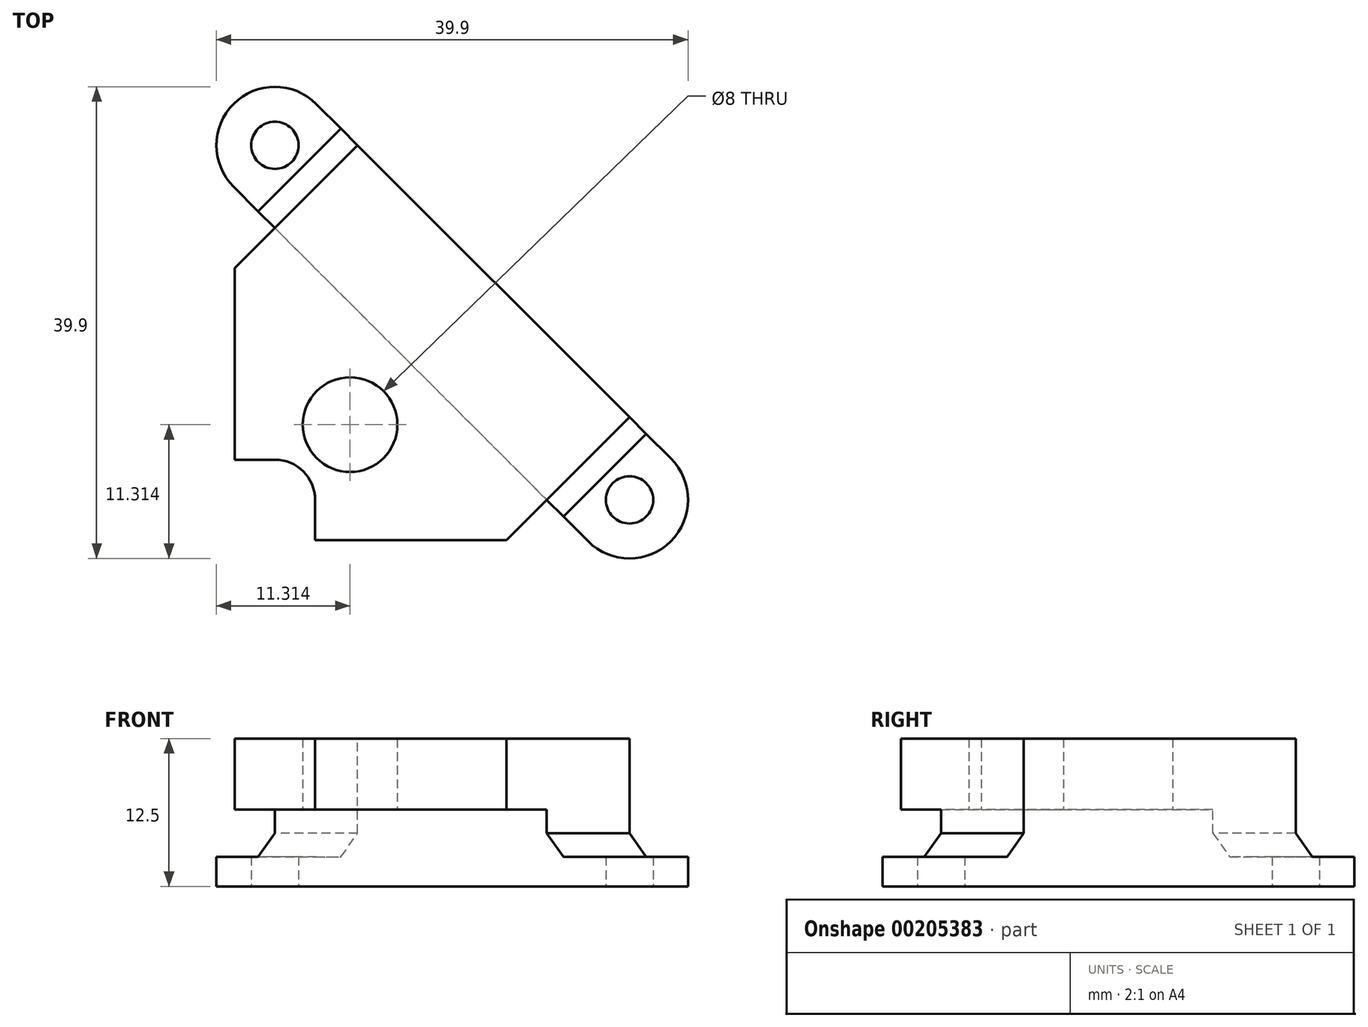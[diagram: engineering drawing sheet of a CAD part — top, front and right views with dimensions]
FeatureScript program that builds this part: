
annotation { "Feature Type Name" : "Feature", "Feature Type Description" : "" }
export const myFeature = defineFeature(function(context is Context, id is Id, definition is map)
    precondition{}
    {
        {
            var Q0;
            Q0=qCreatedBy(makeId("Top.planeOp"),FACE);
            var sketch = newSketch(context, id + "F0", { "sketchPlane" : qUnion([Q0])});
            skLineSegment(sketch, "E0.bottom", {"start": v(0, 0) * mm, "end": v(37, 0) * mm, "construction": true});
            skLineSegment(sketch, "E0.top", {"start": v(0, 37) * mm, "end": v(37, 37) * mm, "construction": true});
            skLineSegment(sketch, "E0.left", {"start": v(0, 0) * mm, "end": v(0, 37) * mm, "construction": true});
            skLineSegment(sketch, "E0.right", {"start": v(37, 0) * mm, "end": v(37, 37) * mm, "construction": true});
            skCircle(sketch, "E1", {"center": v(3.5, 33.5) * mm, "radius": 3 * mm, "construction": true});
            skCircle(sketch, "E2", {"center": v(33.5, 33.5) * mm, "radius": 3 * mm, "construction": true});
            skCircle(sketch, "E3", {"center": v(33.5, 3.5) * mm, "radius": 2.51 * mm, "construction": true});
            skCircle(sketch, "E4", {"center": v(3.5, 3.5) * mm, "radius": 3 * mm, "construction": true});
            skCircle(sketch, "E5", {"center": v(3.5, 33.5) * mm, "radius": 2 * mm});
            skCircle(sketch, "E6", {"center": v(33.5, 3.5) * mm, "radius": 2 * mm});
            skArc(sketch, "E7", {"start": v(7, 37) * mm, "mid": v(0, 37) * mm, "end": v(0, 30) * mm});
            skArc(sketch, "E8", {"start": v(30, 0) * mm, "mid": v(37, 0) * mm, "end": v(37, 7) * mm});
            skLineSegment(sketch, "E9", {"start": v(0, 30) * mm, "end": v(30, 0) * mm});
            skLineSegment(sketch, "E10", {"start": v(7, 37) * mm, "end": v(37, 7) * mm});
            skSolve(sketch);
        }
        {
            var Q0;
            Q0 = qSketchRegion(id + "F0", true);
            extrude(context, id + "F1", {"entities" : qUnion([Q0]), "depth" : 6.5 * mm});
        }
        {
            var Q0;
            Q0=makeQuery(id+"F1.opExtrude","CAP_FACE",FACE,{"disambiguationData":[OSD([sQuery(id+"F0.wireOp",EDGE,"E5"),sQuery(id+"F0.wireOp",EDGE,"E6"),sQuery(id+"F0.wireOp",EDGE,"E7"),sQuery(id+"F0.wireOp",EDGE,"E8"),sQuery(id+"F0.wireOp",EDGE,"E9"),sQuery(id+"F0.wireOp",EDGE,"E10")])],"isStart":false});
            var sketch = newSketch(context, id + "F2", { "sketchPlane" : qUnion([Q0])});
            skArc(sketch, "E11", {"start": v(7, 37) * mm, "mid": v(0, 37) * mm, "end": v(0, 30) * mm});
            skArc(sketch, "E12", {"start": v(30, 0) * mm, "mid": v(37, 0) * mm, "end": v(37, 7) * mm});
            skLineSegment(sketch, "E13", {"start": v(3.5, 26.5) * mm, "end": v(10.5, 33.5) * mm});
            skLineSegment(sketch, "E14", {"start": v(3.5, 26.5) * mm, "end": v(0, 30) * mm});
            skLineSegment(sketch, "E15", {"start": v(10.5, 33.5) * mm, "end": v(7, 37) * mm});
            skLineSegment(sketch, "E16", {"start": v(30, 0) * mm, "end": v(26.5, 3.5) * mm});
            skLineSegment(sketch, "E17", {"start": v(26.5, 3.5) * mm, "end": v(33.5, 10.5) * mm});
            skLineSegment(sketch, "E18", {"start": v(33.5, 10.5) * mm, "end": v(37, 7) * mm});
            skSolve(sketch);
        }
        {
            var Q0;
            Q0 = qSketchRegion(id + "F2", true);
            extrude(context, id + "F3", {"entities" : qUnion([Q0]), "operationType" : NewBodyOperationType.REMOVE, "oppositeDirection" : true, "depth" : 4 * mm});
        }
        {
            var Q0;
            Q0=makeQuery(id+"F1.opExtrude","CAP_FACE",FACE,{"disambiguationData":[OSD([sQuery(id+"F0.wireOp",EDGE,"E5"),sQuery(id+"F0.wireOp",EDGE,"E6"),sQuery(id+"F0.wireOp",EDGE,"E7"),sQuery(id+"F0.wireOp",EDGE,"E8"),sQuery(id+"F0.wireOp",EDGE,"E9"),sQuery(id+"F0.wireOp",EDGE,"E10")])],"isStart":false});
            var sketch = newSketch(context, id + "F4", { "sketchPlane" : qUnion([Q0])});
            skLineSegment(sketch, "E19.bottom", {"start": v(3.5, 33.5) * mm, "end": v(33.5, 33.5) * mm, "construction": true});
            skLineSegment(sketch, "E19.top", {"start": v(3.5, 3.5) * mm, "end": v(33.5, 3.5) * mm, "construction": true});
            skLineSegment(sketch, "E19.left", {"start": v(3.5, 33.5) * mm, "end": v(3.5, 3.5) * mm, "construction": true});
            skLineSegment(sketch, "E19.right", {"start": v(33.5, 33.5) * mm, "end": v(33.5, 3.5) * mm, "construction": true});
            skCircle(sketch, "E20", {"center": v(3.5, 33.5) * mm, "radius": 1.39 * mm, "construction": true});
            skCircle(sketch, "E21", {"center": v(33.5, 3.5) * mm, "radius": 1.3 * mm, "construction": true});
            skArc(sketch, "E22", {"start": v(6.9, 3.5) * mm, "mid": v(5.9, 5.9) * mm, "end": v(3.5, 6.9) * mm});
            skLineSegment(sketch, "E23", {"start": v(33.5, 10.5) * mm, "end": v(10.5, 33.5) * mm});
            skLineSegment(sketch, "E24", {"start": v(10.5, 33.5) * mm, "end": v(0.1, 23.1) * mm});
            skLineSegment(sketch, "E25", {"start": v(33.5, 10.5) * mm, "end": v(23.1, 0.1) * mm});
            skLineSegment(sketch, "E26", {"start": v(6.9, 0.1) * mm, "end": v(23.1, 0.1) * mm});
            skLineSegment(sketch, "E27", {"start": v(0.1, 6.9) * mm, "end": v(0.1, 23.1) * mm});
            skLineSegment(sketch, "E28", {"start": v(3.5, 3.5) * mm, "end": v(33.5, 33.5) * mm, "construction": true});
            skCircle(sketch, "E29", {"center": v(9.86, 9.86) * mm, "radius": 4 * mm});
            skLineSegment(sketch, "E30", {"start": v(3.5, 6.9) * mm, "end": v(0.1, 6.9) * mm});
            skLineSegment(sketch, "E31", {"start": v(6.9, 3.5) * mm, "end": v(6.9, 0) * mm});
            skPoint(sketch, "E32.orphan", {"position": v(3.5, 0.1) * mm});
            skSolve(sketch);
        }
        {
            var Q0;
            Q0 = qSketchRegion(id + "F4", true);
            extrude(context, id + "F5", {"entities" : qUnion([Q0]), "operationType" : NewBodyOperationType.ADD, "depth" : 6 * mm});
        }
        {
            var Q0;
            Q0=makeQuery(id+"F3.boolean.opBoolean","COPY",EDGE,{"derivedFrom":makeQuery(id+"F3.opExtrude","CAP_EDGE",EDGE,{"disambiguationData":[OSD([sQuery(id+"F2.wireOp",EDGE,"E13")])],"isStart":false})});
            var Q1;
            Q1=makeQuery(id+"F1.opExtrude","CAP_EDGE",EDGE,{"disambiguationData":[OSD([sQuery(id+"F0.wireOp",EDGE,"E9")])],"isStart":false});
            var Q2;
            Q2=makeQuery(id+"F3.boolean.opBoolean","COPY",EDGE,{"derivedFrom":makeQuery(id+"F3.opExtrude","CAP_EDGE",EDGE,{"disambiguationData":[OSD([sQuery(id+"F2.wireOp",EDGE,"E17")])],"isStart":false})});
            chamfer(context, id + "F6", {"entities" : qUnion([Q0, Q1, Q2]), "width" : 2 * mm, "tangentPropagation" : true});
        }
    });
